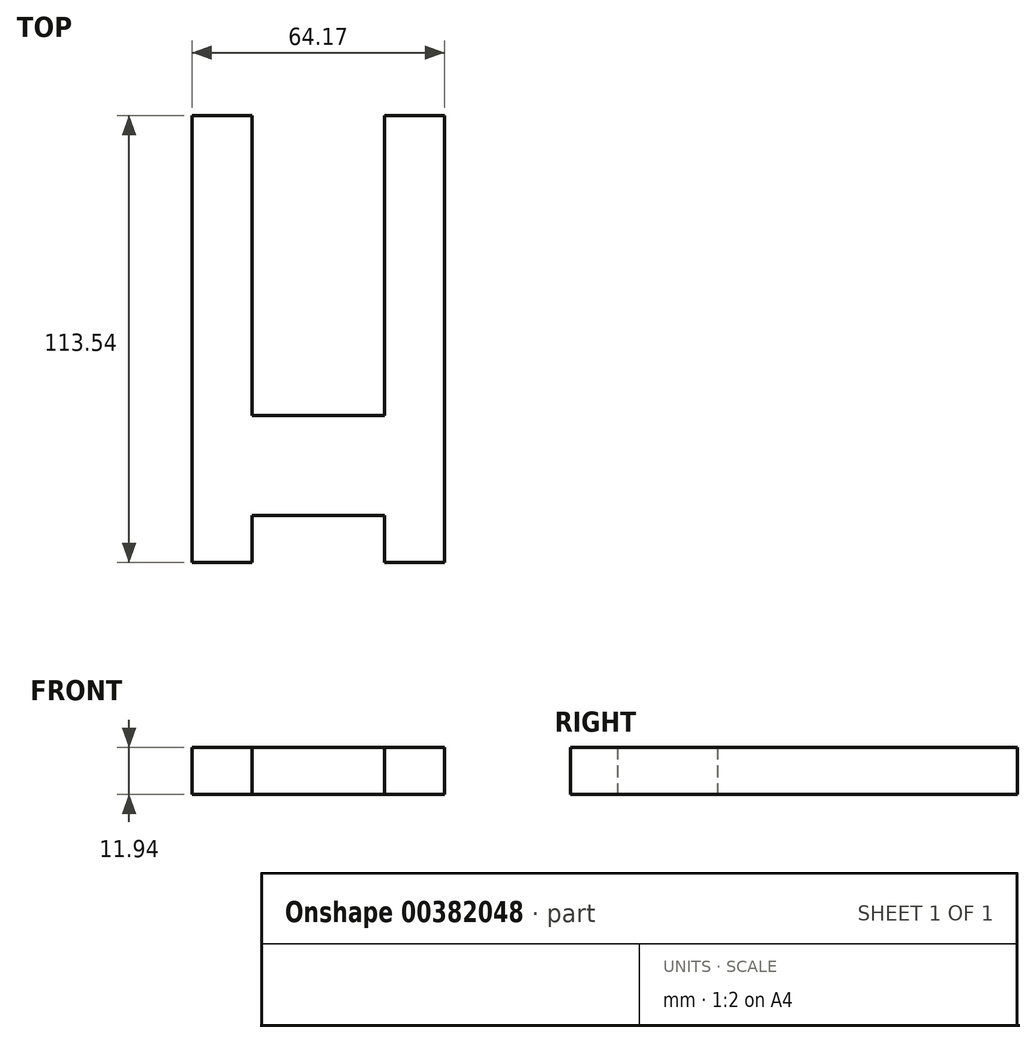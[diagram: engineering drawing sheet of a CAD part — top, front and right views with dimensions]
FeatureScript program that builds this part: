
annotation { "Feature Type Name" : "Feature", "Feature Type Description" : "" }
export const myFeature = defineFeature(function(context is Context, id is Id, definition is map)
    precondition{}
    {
        {
            var Q0;
            Q0=qCreatedBy(makeId("Top.planeOp"),FACE);
            var sketch = newSketch(context, id + "F0", { "sketchPlane" : qUnion([Q0])});
            skLineSegment(sketch, "E0", {"start": v(-26.66, 0) * mm, "end": v(7.03, 0) * mm});
            skLineSegment(sketch, "E1", {"start": v(-41.9, 0) * mm, "end": v(-41.9, 76.2) * mm});
            skLineSegment(sketch, "E2", {"start": v(22.27, 0) * mm, "end": v(22.27, 76.2) * mm});
            skLineSegment(sketch, "E3", {"start": v(22.27, 76.2) * mm, "end": v(7.03, 76.2) * mm});
            skLineSegment(sketch, "E4", {"start": v(-41.9, 76.2) * mm, "end": v(-26.66, 76.2) * mm});
            skLineSegment(sketch, "E5", {"start": v(-26.66, 76.2) * mm, "end": v(-26.66, 0) * mm});
            skLineSegment(sketch, "E6", {"start": v(7.03, 76.2) * mm, "end": v(7.03, 0) * mm});
            skLineSegment(sketch, "E7", {"start": v(-41.9, 0) * mm, "end": v(-41.9, -25.4) * mm});
            skLineSegment(sketch, "E8", {"start": v(22.27, -25.4) * mm, "end": v(22.27, 0) * mm});
            skLineSegment(sketch, "E9", {"start": v(22.27, -37.34) * mm, "end": v(22.27, -25.4) * mm});
            skLineSegment(sketch, "E10", {"start": v(-41.9, -37.34) * mm, "end": v(-41.9, -25.4) * mm});
            skPoint(sketch, "E11.end.orphan", {"position": v(-41.9, -12.7) * mm});
            skPoint(sketch, "E12.end.orphan", {"position": v(0.88, -12.7) * mm});
            skPoint(sketch, "E12.start.orphan", {"position": v(22.27, -12.7) * mm});
            skLineSegment(sketch, "E13", {"start": v(22.27, -37.34) * mm, "end": v(7.03, -37.34) * mm});
            skLineSegment(sketch, "E14", {"start": v(7.03, -37.34) * mm, "end": v(7.03, -25.4) * mm});
            skLineSegment(sketch, "E15", {"start": v(7.03, -25.4) * mm, "end": v(-26.67, -25.4) * mm});
            skLineSegment(sketch, "E16", {"start": v(-26.67, -25.4) * mm, "end": v(-26.67, -37.34) * mm});
            skLineSegment(sketch, "E17", {"start": v(-26.67, -37.34) * mm, "end": v(-41.9, -37.34) * mm});
            skSolve(sketch);
        }
        {
            var Q0;
            Q0=makeQuery(id+"F0.imprint","IMPRINT",FACE,{"disambiguationData":[TD([[makeQuery(id+"F0.imprint","IMPRINT",EDGE,{"derivedFrom":sQuery(id+"F0.wireOp",EDGE,"E0")}),-1.0]])]});
            extrude(context, id + "F1", {"entities" : qUnion([Q0]), "depth" : 11.94 * mm});
        }
    });
